# Revit family: EKF_EE_КомплектПластронов200UNIT_PROxima
name_source: partatom
category: Электрооборудование
units: mm (PartAtom-declared; Revit-internal decimal feet)

## family parameters
Всегда вертикально = Нет
На основе рабочей плоскости = Да
Общий = Да
При загрузке вырезать с полостями = Нет
Размер круглого соединителя = Использовать диаметр
Тип детали = Силовой щит
Точка расчета площади = Нет

## types (3) — shared parameters
ADSK_Единица измерения = шт.
ADSK_Завод-изготовитель = EKF
ADSK_Количество = 1
ADSK_Марка = Комплект пластронов (3шт.)
ADSK_Материал = Сталь, с порошковым покрытием, белый
ADSK_Обозначение = Комплект пластронов (3шт.)
ADSK_Размер_Высота = 198 мм
ADSK_Размер_Глубина = 8 мм
D = 7 мм
t = 1.2 мм
Высота = 193 мм
Глубина = 8 мм
Изготовитель = EKF
Отв_b = 46 мм
Отв_Кол = 2
Отступ = 11 мм
ОтступВ = 24 мм
Серия номенклатуры = Unit PROxima
Степень защиты IP = -
ТВ = EKF_2
Тип установки = -
zero-valued in all types: Отметка по умолчанию

## per-type parameters (varying)
| type | ADSK_Код изделия | ADSK_Масса | ADSK_Размер_Ширина | n | Тип |
| Комплект пластронов (3шт.) высотой 200мм под 1 уровень мод. авт. для ВРУ Unit шириной 450мм EKF PROxima | mb-15-mp-2045 | 0.45 | 332 мм | 248 мм | 21 мм |
| Комплект пластронов (3шт.) высотой 200мм под 1 уровень мод. авт. для ВРУ Unit шириной 600мм EKF PROxima | mb-15-mp-2060 | 0.644 | 482 мм | 398 мм | 22 мм |
| Комплект пластронов (3шт.) высотой 200мм под 1 уровень мод. авт. для ВРУ Unit шириной 800мм EKF PROxima | mb-15-mp-2080 | 0.902 | 682 мм | 598 мм | 23 мм |

note: column(s) folded — value = type name in every type: ADSK_Наименование
